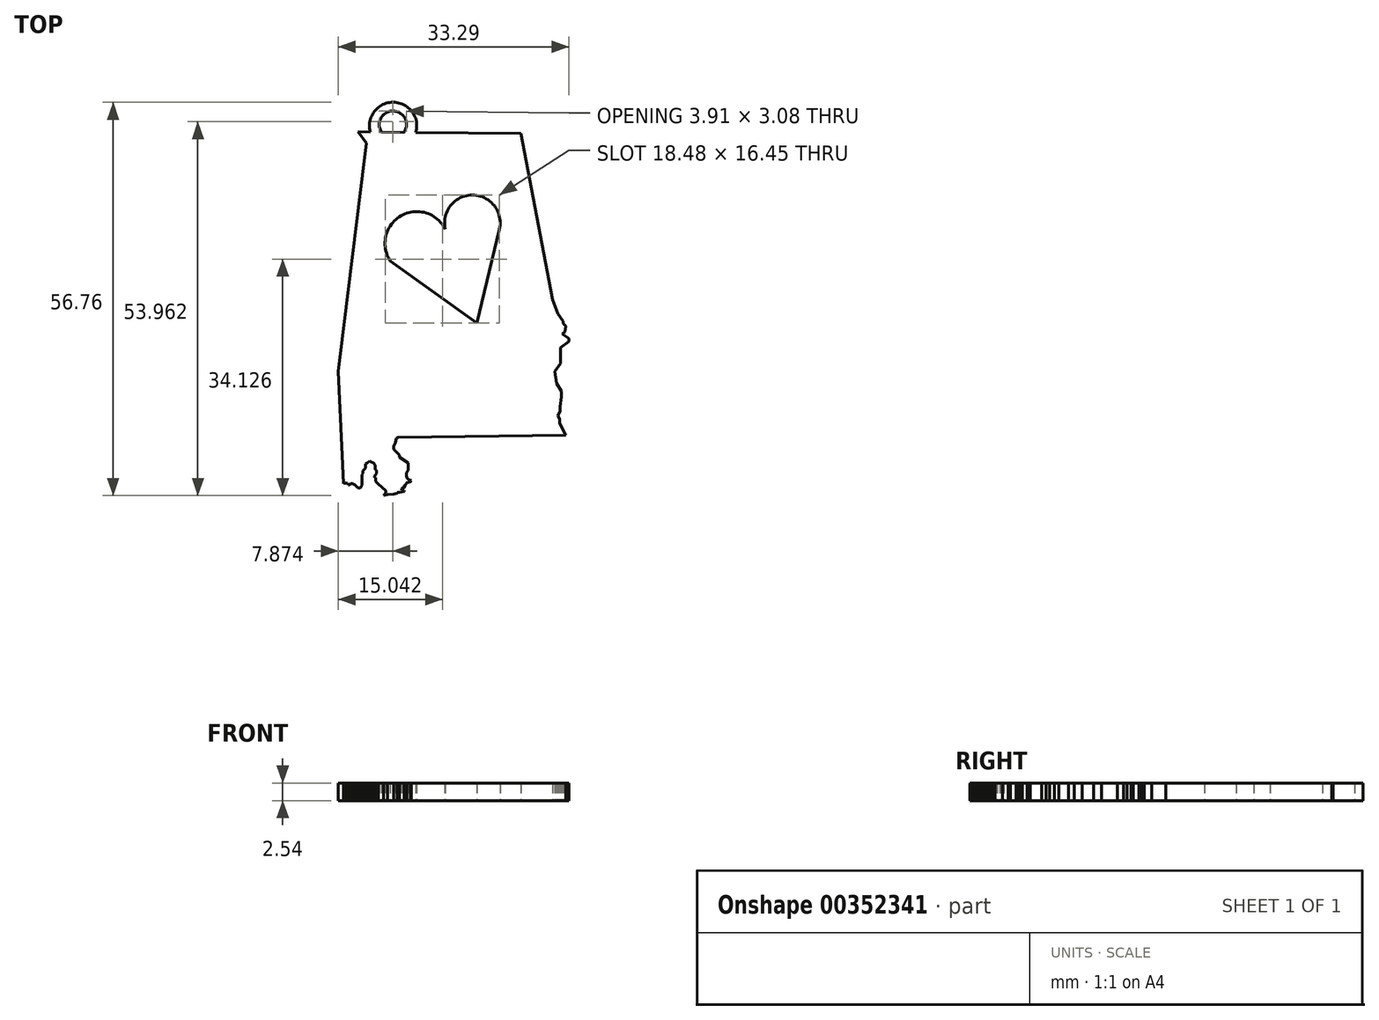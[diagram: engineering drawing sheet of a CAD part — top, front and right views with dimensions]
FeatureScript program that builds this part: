
annotation { "Feature Type Name" : "Feature", "Feature Type Description" : "" }
export const myFeature = defineFeature(function(context is Context, id is Id, definition is map)
    precondition{}
    {
        {
            var Q0;
            Q0=qCreatedBy(makeId("Top.planeOp"),FACE);
            var sketch = newSketch(context, id + "F0", { "sketchPlane" : qUnion([Q0])});
            skPoint(sketch, "E0.middle", {"position": v(0, 0) * mm});
            skLineSegment(sketch, "E1", {"start": v(-14.78, 23.27) * mm, "end": v(-13.03, 23.25) * mm});
            skLineSegment(sketch, "E2", {"start": v(8.72, 23.03) * mm, "end": v(13.28, -0.93) * mm});
            skLineSegment(sketch, "E3", {"start": v(13.28, -0.93) * mm, "end": v(14.02, -2.97) * mm});
            skLineSegment(sketch, "E4", {"start": v(14.02, -2.97) * mm, "end": v(14.82, -4.06) * mm});
            skLineSegment(sketch, "E5", {"start": v(14.82, -4.06) * mm, "end": v(14.82, -4.4) * mm});
            skLineSegment(sketch, "E6", {"start": v(14.82, -4.4) * mm, "end": v(15.14, -4.8) * mm});
            skLineSegment(sketch, "E7", {"start": v(15.14, -4.8) * mm, "end": v(15.05, -5.62) * mm});
            skLineSegment(sketch, "E8", {"start": v(15.05, -5.62) * mm, "end": v(14.69, -5.92) * mm});
            skLineSegment(sketch, "E9", {"start": v(14.69, -5.92) * mm, "end": v(15.64, -6.52) * mm});
            skLineSegment(sketch, "E10", {"start": v(15.64, -6.52) * mm, "end": v(15.64, -7.02) * mm});
            skLineSegment(sketch, "E11", {"start": v(15.64, -7.02) * mm, "end": v(14.42, -7.9) * mm});
            skLineSegment(sketch, "E12", {"start": v(14.42, -7.9) * mm, "end": v(14.42, -10.2) * mm});
            skLineSegment(sketch, "E13", {"start": v(14.42, -10.2) * mm, "end": v(13.6, -11.34) * mm});
            skLineSegment(sketch, "E14", {"start": v(13.6, -11.34) * mm, "end": v(13.85, -13) * mm});
            skLineSegment(sketch, "E15", {"start": v(13.85, -13) * mm, "end": v(14.53, -14.14) * mm});
            skLineSegment(sketch, "E16", {"start": v(14.53, -14.14) * mm, "end": v(14.53, -15) * mm});
            skLineSegment(sketch, "E17", {"start": v(14.53, -15) * mm, "end": v(14.33, -16.39) * mm});
            skLineSegment(sketch, "E18", {"start": v(14.33, -16.39) * mm, "end": v(14.33, -17) * mm});
            skLineSegment(sketch, "E19", {"start": v(14.33, -17) * mm, "end": v(14.05, -17.72) * mm});
            skLineSegment(sketch, "E20", {"start": v(14.05, -17.72) * mm, "end": v(14.27, -18.18) * mm});
            skLineSegment(sketch, "E21", {"start": v(14.27, -18.18) * mm, "end": v(14.27, -18.83) * mm});
            skLineSegment(sketch, "E22", {"start": v(14.27, -18.83) * mm, "end": v(15.17, -20.5) * mm});
            skLineSegment(sketch, "E23", {"start": v(15.17, -20.5) * mm, "end": v(-9.04, -20.86) * mm});
            skLineSegment(sketch, "E24", {"start": v(-9.04, -20.86) * mm, "end": v(-9.24, -20.97) * mm});
            skLineSegment(sketch, "E25", {"start": v(-9.24, -20.97) * mm, "end": v(-9.39, -21.6) * mm});
            skLineSegment(sketch, "E26", {"start": v(-9.39, -21.6) * mm, "end": v(-9.65, -22.11) * mm});
            skLineSegment(sketch, "E27", {"start": v(-9.65, -22.11) * mm, "end": v(-9.65, -22.54) * mm});
            skLineSegment(sketch, "E28", {"start": v(-9.65, -22.54) * mm, "end": v(-8.81, -23.37) * mm});
            skLineSegment(sketch, "E29", {"start": v(-8.81, -23.37) * mm, "end": v(-8.81, -23.68) * mm});
            skLineSegment(sketch, "E30", {"start": v(-8.81, -23.68) * mm, "end": v(-7.55, -24.52) * mm});
            skLineSegment(sketch, "E31", {"start": v(-7.55, -24.52) * mm, "end": v(-7.55, -25.58) * mm});
            skLineSegment(sketch, "E32", {"start": v(-7.55, -25.58) * mm, "end": v(-7.82, -25.93) * mm});
            skLineSegment(sketch, "E33", {"start": v(-7.82, -25.93) * mm, "end": v(-7.82, -26.38) * mm});
            skLineSegment(sketch, "E34", {"start": v(-7.82, -26.38) * mm, "end": v(-7.73, -26.69) * mm});
            skLineSegment(sketch, "E35", {"start": v(-7.73, -26.69) * mm, "end": v(-7.46, -26.9) * mm});
            skLineSegment(sketch, "E36", {"start": v(-7.46, -26.9) * mm, "end": v(-7.13, -27.05) * mm});
            skLineSegment(sketch, "E37", {"start": v(-7.13, -27.05) * mm, "end": v(-7.23, -27.27) * mm});
            skLineSegment(sketch, "E38", {"start": v(-7.23, -27.27) * mm, "end": v(-7.75, -27.36) * mm});
            skLineSegment(sketch, "E39", {"start": v(-7.75, -27.36) * mm, "end": v(-8.01, -27.76) * mm});
            skLineSegment(sketch, "E40", {"start": v(-8.01, -27.76) * mm, "end": v(-8.2, -28.1) * mm});
            skLineSegment(sketch, "E41", {"start": v(-8.2, -28.1) * mm, "end": v(-8.49, -28.24) * mm});
            skLineSegment(sketch, "E42", {"start": v(-8.49, -28.24) * mm, "end": v(-8.49, -28.45) * mm});
            skLineSegment(sketch, "E43", {"start": v(-8.49, -28.45) * mm, "end": v(-8.12, -28.54) * mm});
            skLineSegment(sketch, "E44", {"start": v(-8.12, -28.54) * mm, "end": v(-8.12, -28.63) * mm});
            skLineSegment(sketch, "E45", {"start": v(-8.12, -28.63) * mm, "end": v(-8.81, -28.74) * mm});
            skLineSegment(sketch, "E46", {"start": v(-8.81, -28.74) * mm, "end": v(-9.17, -28.74) * mm});
            skLineSegment(sketch, "E47", {"start": v(-9.17, -28.74) * mm, "end": v(-9.17, -28.9) * mm});
            skLineSegment(sketch, "E48", {"start": v(-9.17, -28.9) * mm, "end": v(-9.65, -29.02) * mm});
            skLineSegment(sketch, "E49", {"start": v(-9.65, -29.02) * mm, "end": v(-10.55, -29.09) * mm});
            skLineSegment(sketch, "E50", {"start": v(-10.55, -29.09) * mm, "end": v(-11.1, -29.22) * mm});
            skLineSegment(sketch, "E51", {"start": v(-11.1, -29.22) * mm, "end": v(-10.79, -28.85) * mm});
            skLineSegment(sketch, "E52", {"start": v(-10.79, -28.85) * mm, "end": v(-10.79, -28.54) * mm});
            skLineSegment(sketch, "E53", {"start": v(-10.79, -28.54) * mm, "end": v(-11.87, -27.58) * mm});
            skLineSegment(sketch, "E54", {"start": v(-11.87, -27.58) * mm, "end": v(-12.26, -27.2) * mm});
            skLineSegment(sketch, "E55", {"start": v(-12.26, -27.2) * mm, "end": v(-12.26, -26.66) * mm});
            skLineSegment(sketch, "E56", {"start": v(-12.26, -26.66) * mm, "end": v(-12.42, -26.55) * mm});
            skLineSegment(sketch, "E57", {"start": v(-12.42, -26.55) * mm, "end": v(-12.42, -26.46) * mm});
            skLineSegment(sketch, "E58", {"start": v(-12.42, -26.46) * mm, "end": v(-12.15, -26.04) * mm});
            skLineSegment(sketch, "E59", {"start": v(-12.15, -26.04) * mm, "end": v(-12.15, -25.58) * mm});
            skLineSegment(sketch, "E60", {"start": v(-12.15, -25.58) * mm, "end": v(-12.32, -25.49) * mm});
            skLineSegment(sketch, "E61", {"start": v(-12.32, -25.49) * mm, "end": v(-12.32, -24.85) * mm});
            skLineSegment(sketch, "E62", {"start": v(-12.32, -24.85) * mm, "end": v(-12.6, -24.52) * mm});
            skLineSegment(sketch, "E63", {"start": v(-12.6, -24.52) * mm, "end": v(-12.9, -24.4) * mm});
            skLineSegment(sketch, "E64", {"start": v(-12.9, -24.4) * mm, "end": v(-13.15, -24.28) * mm});
            skLineSegment(sketch, "E65", {"start": v(-13.15, -24.28) * mm, "end": v(-13.44, -24.52) * mm});
            skLineSegment(sketch, "E66", {"start": v(-13.44, -24.52) * mm, "end": v(-13.7, -24.66) * mm});
            skLineSegment(sketch, "E67", {"start": v(-13.7, -24.66) * mm, "end": v(-13.7, -24.88) * mm});
            skLineSegment(sketch, "E68", {"start": v(-13.7, -24.88) * mm, "end": v(-13.7, -25.27) * mm});
            skLineSegment(sketch, "E69", {"start": v(-13.7, -25.27) * mm, "end": v(-13.92, -25.49) * mm});
            skLineSegment(sketch, "E70", {"start": v(-13.92, -25.49) * mm, "end": v(-14.09, -25.67) * mm});
            skLineSegment(sketch, "E71", {"start": v(-14.09, -25.67) * mm, "end": v(-14.09, -26.04) * mm});
            skLineSegment(sketch, "E72", {"start": v(-14.09, -26.04) * mm, "end": v(-14.23, -26.24) * mm});
            skLineSegment(sketch, "E73", {"start": v(-14.23, -26.24) * mm, "end": v(-14.23, -27.76) * mm});
            skLineSegment(sketch, "E74", {"start": v(-14.23, -27.76) * mm, "end": v(-14.45, -28.14) * mm});
            skLineSegment(sketch, "E75", {"start": v(-14.45, -28.14) * mm, "end": v(-14.77, -28.14) * mm});
            skLineSegment(sketch, "E76", {"start": v(-14.77, -28.14) * mm, "end": v(-15.2, -27.66) * mm});
            skLineSegment(sketch, "E77", {"start": v(-15.2, -27.66) * mm, "end": v(-15.64, -27.51) * mm});
            skLineSegment(sketch, "E78", {"start": v(-15.64, -27.51) * mm, "end": v(-15.85, -27.51) * mm});
            skLineSegment(sketch, "E79", {"start": v(-15.85, -27.51) * mm, "end": v(-15.98, -27.66) * mm});
            skLineSegment(sketch, "E80", {"start": v(-15.98, -27.66) * mm, "end": v(-16.17, -27.66) * mm});
            skLineSegment(sketch, "E81", {"start": v(-16.17, -27.66) * mm, "end": v(-16.34, -27.46) * mm});
            skLineSegment(sketch, "E82", {"start": v(-16.34, -27.46) * mm, "end": v(-16.78, -27.46) * mm});
            skLineSegment(sketch, "E83", {"start": v(-16.78, -27.46) * mm, "end": v(-16.86, -27.53) * mm});
            skLineSegment(sketch, "E84", {"start": v(-16.86, -27.53) * mm, "end": v(-17.65, -11.28) * mm});
            skLineSegment(sketch, "E85", {"start": v(-17.65, -11.28) * mm, "end": v(-13.6, 21.67) * mm});
            skLineSegment(sketch, "E86", {"start": v(-13.6, 21.67) * mm, "end": v(-14.78, 23.27) * mm});
            skArc(sketch, "E87", {"start": v(-8.17, 23.2) * mm, "mid": v(-9.76, 26.28) * mm, "end": v(-11.4, 23.23) * mm});
            skLineSegment(sketch, "E88.trimOffspring", {"start": v(-11.4, 23.23) * mm, "end": v(-8.17, 23.2) * mm});
            skLineSegment(sketch, "E89.trimOffspring", {"start": v(-6.45, 23.18) * mm, "end": v(8.72, 23.03) * mm});
            skPoint(sketch, "E90.end.orphan", {"position": v(-8.49, 18.15) * mm});
            skLineSegment(sketch, "E91", {"start": v(5.6, 9.2) * mm, "end": v(2.36, -4.33) * mm});
            skLineSegment(sketch, "E92", {"start": v(2.36, -4.33) * mm, "end": v(-10.14, 4.64) * mm});
            skPoint(sketch, "E93.end.orphan", {"position": v(-2.2, 9.2) * mm});
            skArc(sketch, "E94", {"start": v(-2.2, 9.2) * mm, "mid": v(-8.6, 11.16) * mm, "end": v(-10.14, 4.64) * mm});
            skArc(sketch, "E95", {"start": v(5.6, 9.2) * mm, "mid": v(1.7, 14.15) * mm, "end": v(-2.2, 9.2) * mm});
            skArc(sketch, "E96.0", {"start": v(-6.45, 23.18) * mm, "mid": v(-9.7, 27.54) * mm, "end": v(-13.03, 23.25) * mm});
            skSolve(sketch);
        }
        {
            var Q0;
            Q0=makeQuery(id+"F0.imprint","IMPRINT",FACE,{"disambiguationData":[TD([[makeQuery(id+"F0.imprint","IMPRINT",EDGE,{"derivedFrom":sQuery(id+"F0.wireOp",EDGE,"E1")}),-1.0]])]});
            extrude(context, id + "F1", {"entities" : qUnion([Q0]), "depth" : 2.54 * mm});
        }
    });
